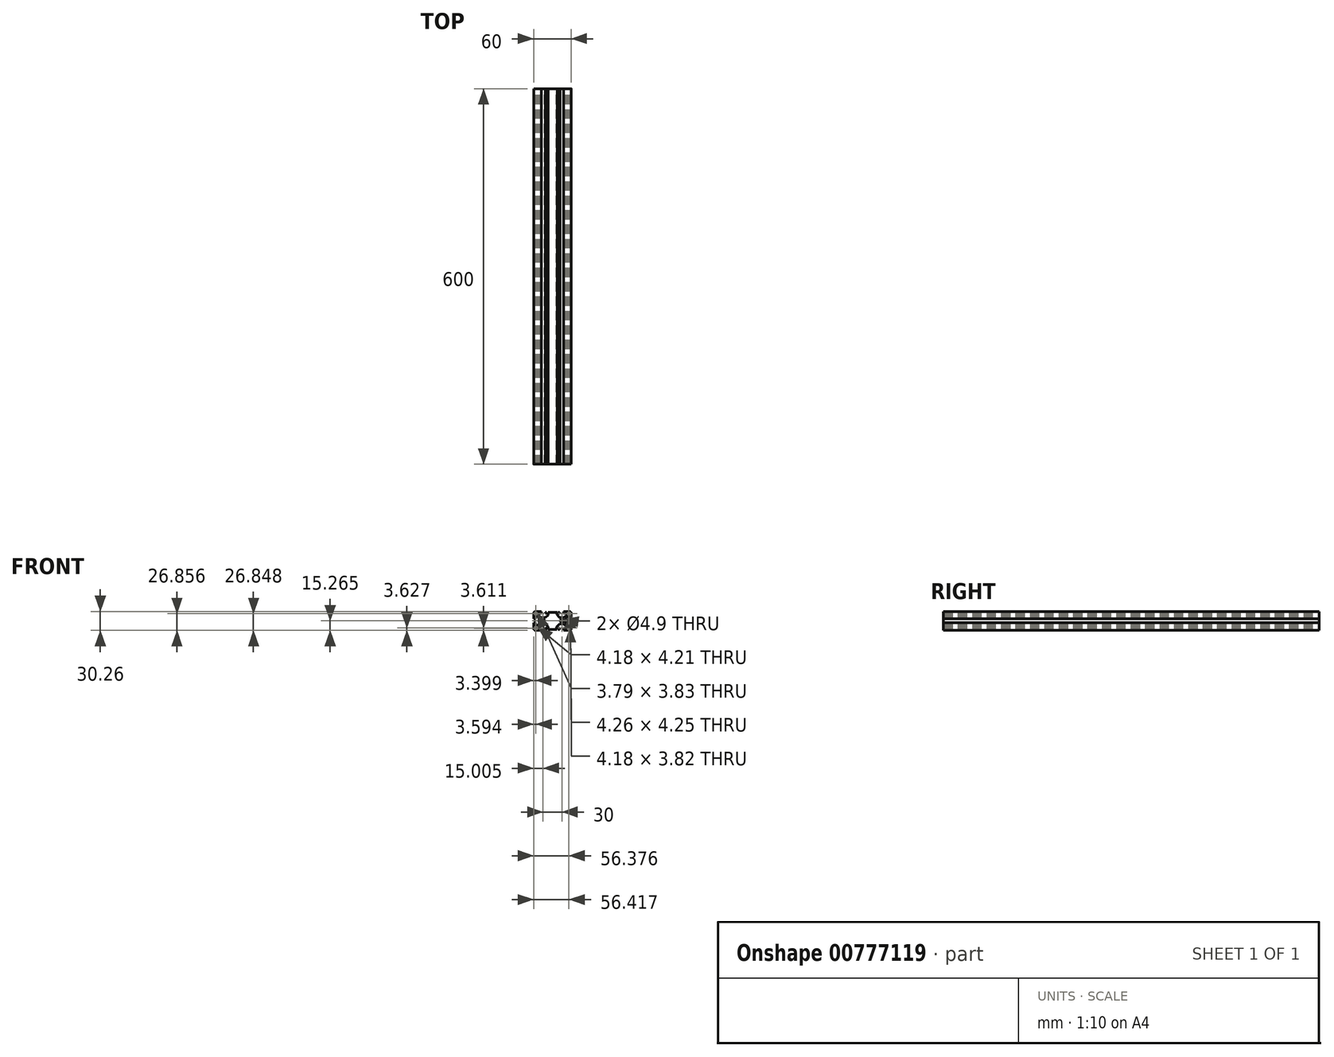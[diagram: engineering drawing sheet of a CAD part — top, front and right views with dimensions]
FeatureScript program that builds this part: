
annotation { "Feature Type Name" : "Feature", "Feature Type Description" : "" }
export const myFeature = defineFeature(function(context is Context, id is Id, definition is map)
    precondition{}
    {
        {
            var Q0;
            Q0=qCreatedBy(makeId("Front.planeOp"),FACE);
            var sketch = newSketch(context, id + "F0", { "sketchPlane" : qUnion([Q0])});
            skLineSegment(sketch, "E0.bottom", {"start": v(-62.13, 53.63) * mm, "end": v(-8.13, 53.63) * mm});
            skLineSegment(sketch, "E0.top", {"start": v(-62.13, 23.37) * mm, "end": v(-8.13, 23.37) * mm});
            skLineSegment(sketch, "E0.left", {"start": v(-65.13, 50.63) * mm, "end": v(-65.13, 26.37) * mm});
            skLineSegment(sketch, "E0.right", {"start": v(-5.13, 50.63) * mm, "end": v(-5.13, 26.37) * mm});
            skPoint(sketch, "E1.visualSharp", {"position": v(-65.13, 53.63) * mm});
            skArc(sketch, "E1.filletArc", {"start": v(-62.13, 53.63) * mm, "mid": v(-64.25, 52.76) * mm, "end": v(-65.13, 50.63) * mm});
            skPoint(sketch, "E2.visualSharp", {"position": v(-5.13, 53.63) * mm});
            skArc(sketch, "E2.filletArc", {"start": v(-5.13, 50.63) * mm, "mid": v(-6, 52.76) * mm, "end": v(-8.13, 53.63) * mm});
            skPoint(sketch, "E3.visualSharp", {"position": v(-5.13, 23.37) * mm});
            skArc(sketch, "E3.filletArc", {"start": v(-8.13, 23.37) * mm, "mid": v(-6, 24.25) * mm, "end": v(-5.13, 26.37) * mm});
            skPoint(sketch, "E4.visualSharp", {"position": v(-65.13, 23.37) * mm});
            skArc(sketch, "E4.filletArc", {"start": v(-65.13, 26.37) * mm, "mid": v(-64.25, 24.25) * mm, "end": v(-62.13, 23.37) * mm});
            skCircle(sketch, "E5", {"center": v(-50.13, 38.63) * mm, "radius": 2.45 * mm});
            skCircle(sketch, "E6", {"center": v(-20.13, 38.63) * mm, "radius": 2.45 * mm});
            skLineSegment(sketch, "E7.bottom", {"start": v(-62.63, 52.13) * mm, "end": v(-7.63, 52.13) * mm});
            skLineSegment(sketch, "E7.top", {"start": v(-62.63, 24.87) * mm, "end": v(-7.53, 24.87) * mm});
            skLineSegment(sketch, "E7.left", {"start": v(-63.63, 51.13) * mm, "end": v(-63.63, 25.87) * mm});
            skLineSegment(sketch, "E7.right", {"start": v(-6.63, 51.13) * mm, "end": v(-6.63, 25.77) * mm});
            skPoint(sketch, "E8.visualSharp", {"position": v(-6.63, 52.13) * mm});
            skArc(sketch, "E8.filletArc", {"start": v(-6.63, 51.13) * mm, "mid": v(-6.92, 51.84) * mm, "end": v(-7.63, 52.13) * mm});
            skPoint(sketch, "E9.visualSharp", {"position": v(-6.63, 24.87) * mm});
            skArc(sketch, "E9.filletArc", {"start": v(-7.53, 24.87) * mm, "mid": v(-6.89, 25.14) * mm, "end": v(-6.63, 25.77) * mm});
            skPoint(sketch, "E10.visualSharp", {"position": v(-63.63, 24.87) * mm});
            skArc(sketch, "E10.filletArc", {"start": v(-63.63, 25.87) * mm, "mid": v(-63.33, 25.17) * mm, "end": v(-62.63, 24.87) * mm});
            skPoint(sketch, "E11.visualSharp", {"position": v(-63.63, 52.13) * mm});
            skArc(sketch, "E11.filletArc", {"start": v(-62.63, 52.13) * mm, "mid": v(-63.33, 51.84) * mm, "end": v(-63.63, 51.13) * mm});
            skLineSegment(sketch, "E12.bottom", {"start": v(-59.84, 48.3) * mm, "end": v(-63.63, 48.3) * mm});
            skLineSegment(sketch, "E12.top", {"start": v(-59.84, 52.13) * mm, "end": v(-63.63, 52.13) * mm});
            skLineSegment(sketch, "E12.left", {"start": v(-59.84, 48.3) * mm, "end": v(-59.84, 52.13) * mm});
            skLineSegment(sketch, "E12.right", {"start": v(-63.63, 48.3) * mm, "end": v(-63.63, 52.13) * mm});
            skLineSegment(sketch, "E13.bottom", {"start": v(-59.45, 29.09) * mm, "end": v(-63.63, 29.09) * mm});
            skLineSegment(sketch, "E13.top", {"start": v(-59.45, 24.87) * mm, "end": v(-63.63, 24.87) * mm});
            skLineSegment(sketch, "E13.left", {"start": v(-59.45, 29.09) * mm, "end": v(-59.45, 24.87) * mm});
            skLineSegment(sketch, "E13.right", {"start": v(-63.63, 29.09) * mm, "end": v(-63.63, 24.87) * mm});
            skLineSegment(sketch, "E14.bottom", {"start": v(-10.88, 29.12) * mm, "end": v(-6.63, 29.12) * mm});
            skLineSegment(sketch, "E14.top", {"start": v(-10.88, 24.87) * mm, "end": v(-6.63, 24.87) * mm});
            skLineSegment(sketch, "E14.left", {"start": v(-10.88, 29.12) * mm, "end": v(-10.88, 24.87) * mm});
            skLineSegment(sketch, "E14.right", {"start": v(-6.63, 29.12) * mm, "end": v(-6.63, 24.87) * mm});
            skLineSegment(sketch, "E15.bottom", {"start": v(-6.63, 52.13) * mm, "end": v(-10.8, 52.13) * mm});
            skLineSegment(sketch, "E15.top", {"start": v(-6.63, 48.32) * mm, "end": v(-10.8, 48.32) * mm});
            skLineSegment(sketch, "E15.left", {"start": v(-6.63, 52.13) * mm, "end": v(-6.63, 48.32) * mm});
            skLineSegment(sketch, "E15.right", {"start": v(-10.8, 52.13) * mm, "end": v(-10.8, 48.32) * mm});
            skLineSegment(sketch, "E16.bottom", {"start": v(-55.91, 50.63) * mm, "end": v(-53.07, 50.63) * mm});
            skLineSegment(sketch, "E16.top", {"start": v(-55.91, 52.13) * mm, "end": v(-53.07, 52.13) * mm});
            skLineSegment(sketch, "E16.left", {"start": v(-55.91, 50.63) * mm, "end": v(-55.91, 52.13) * mm});
            skLineSegment(sketch, "E16.right", {"start": v(-53.07, 50.63) * mm, "end": v(-53.07, 52.13) * mm});
            skLineSegment(sketch, "E17.bottom", {"start": v(-44.63, 50.63) * mm, "end": v(-46.61, 50.63) * mm});
            skLineSegment(sketch, "E17.top", {"start": v(-44.63, 52.13) * mm, "end": v(-46.61, 52.13) * mm});
            skLineSegment(sketch, "E17.left", {"start": v(-44.63, 50.63) * mm, "end": v(-44.63, 52.13) * mm});
            skLineSegment(sketch, "E17.right", {"start": v(-46.61, 50.63) * mm, "end": v(-46.61, 52.13) * mm});
            skLineSegment(sketch, "E18.bottom", {"start": v(-26.48, 50.63) * mm, "end": v(-23.47, 50.63) * mm});
            skLineSegment(sketch, "E18.top", {"start": v(-26.48, 52.13) * mm, "end": v(-23.47, 52.13) * mm});
            skLineSegment(sketch, "E18.left", {"start": v(-26.48, 50.63) * mm, "end": v(-26.48, 52.13) * mm});
            skLineSegment(sketch, "E18.right", {"start": v(-23.47, 50.63) * mm, "end": v(-23.47, 52.13) * mm});
            skLineSegment(sketch, "E19.bottom", {"start": v(-14.95, 50.63) * mm, "end": v(-17.1, 50.63) * mm});
            skLineSegment(sketch, "E19.top", {"start": v(-14.95, 52.13) * mm, "end": v(-17.1, 52.13) * mm});
            skLineSegment(sketch, "E19.left", {"start": v(-14.95, 50.63) * mm, "end": v(-14.95, 52.13) * mm});
            skLineSegment(sketch, "E19.right", {"start": v(-17.1, 50.63) * mm, "end": v(-17.1, 52.13) * mm});
            skLineSegment(sketch, "E20.bottom", {"start": v(-8.13, 44.16) * mm, "end": v(-6.63, 44.16) * mm});
            skLineSegment(sketch, "E20.top", {"start": v(-8.13, 41.83) * mm, "end": v(-6.63, 41.83) * mm});
            skLineSegment(sketch, "E20.left", {"start": v(-8.13, 44.16) * mm, "end": v(-8.13, 41.83) * mm});
            skLineSegment(sketch, "E20.right", {"start": v(-6.63, 44.16) * mm, "end": v(-6.63, 41.83) * mm});
            skLineSegment(sketch, "E21.bottom", {"start": v(-8.13, 32.88) * mm, "end": v(-6.63, 32.88) * mm});
            skLineSegment(sketch, "E21.top", {"start": v(-8.13, 35.38) * mm, "end": v(-6.63, 35.38) * mm});
            skLineSegment(sketch, "E21.left", {"start": v(-8.13, 32.88) * mm, "end": v(-8.13, 35.38) * mm});
            skLineSegment(sketch, "E21.right", {"start": v(-6.63, 32.88) * mm, "end": v(-6.63, 35.38) * mm});
            skLineSegment(sketch, "E22.bottom", {"start": v(-14.8, 26.37) * mm, "end": v(-17.1, 26.37) * mm});
            skLineSegment(sketch, "E22.top", {"start": v(-14.8, 24.87) * mm, "end": v(-17.1, 24.87) * mm});
            skLineSegment(sketch, "E22.left", {"start": v(-14.8, 26.37) * mm, "end": v(-14.8, 24.87) * mm});
            skLineSegment(sketch, "E22.right", {"start": v(-17.1, 26.37) * mm, "end": v(-17.1, 24.87) * mm});
            skLineSegment(sketch, "E23.bottom", {"start": v(-26.1, 26.37) * mm, "end": v(-23.56, 26.37) * mm});
            skLineSegment(sketch, "E23.top", {"start": v(-26.1, 24.87) * mm, "end": v(-23.56, 24.87) * mm});
            skLineSegment(sketch, "E23.left", {"start": v(-26.1, 26.37) * mm, "end": v(-26.1, 24.87) * mm});
            skLineSegment(sketch, "E23.right", {"start": v(-23.56, 26.37) * mm, "end": v(-23.56, 24.87) * mm});
            skLineSegment(sketch, "E24.bottom", {"start": v(-44.16, 26.37) * mm, "end": v(-46.61, 26.37) * mm});
            skLineSegment(sketch, "E24.top", {"start": v(-44.16, 24.87) * mm, "end": v(-46.61, 24.87) * mm});
            skLineSegment(sketch, "E24.left", {"start": v(-44.16, 26.37) * mm, "end": v(-44.16, 24.87) * mm});
            skLineSegment(sketch, "E24.right", {"start": v(-46.61, 26.37) * mm, "end": v(-46.61, 24.87) * mm});
            skLineSegment(sketch, "E25.bottom", {"start": v(-55.52, 26.37) * mm, "end": v(-53.07, 26.37) * mm});
            skLineSegment(sketch, "E25.top", {"start": v(-55.52, 24.87) * mm, "end": v(-53.07, 24.87) * mm});
            skLineSegment(sketch, "E25.left", {"start": v(-55.52, 26.37) * mm, "end": v(-55.52, 24.87) * mm});
            skLineSegment(sketch, "E25.right", {"start": v(-53.07, 26.37) * mm, "end": v(-53.07, 24.87) * mm});
            skLineSegment(sketch, "E26.bottom", {"start": v(-62.13, 33.01) * mm, "end": v(-63.63, 33.01) * mm});
            skLineSegment(sketch, "E26.top", {"start": v(-62.13, 35.38) * mm, "end": v(-63.63, 35.38) * mm});
            skLineSegment(sketch, "E26.left", {"start": v(-62.13, 33.01) * mm, "end": v(-62.13, 35.38) * mm});
            skLineSegment(sketch, "E26.right", {"start": v(-63.63, 33.01) * mm, "end": v(-63.63, 35.38) * mm});
            skLineSegment(sketch, "E27.bottom", {"start": v(-62.13, 44.3) * mm, "end": v(-63.63, 44.3) * mm});
            skLineSegment(sketch, "E27.top", {"start": v(-62.13, 41.83) * mm, "end": v(-63.63, 41.83) * mm});
            skLineSegment(sketch, "E27.left", {"start": v(-62.13, 44.3) * mm, "end": v(-62.13, 41.83) * mm});
            skLineSegment(sketch, "E27.right", {"start": v(-63.63, 44.3) * mm, "end": v(-63.63, 41.83) * mm});
            skLineSegment(sketch, "E28", {"start": v(-57.98, 52.13) * mm, "end": v(-57.98, 48.56) * mm});
            skLineSegment(sketch, "E29", {"start": v(-57.98, 48.56) * mm, "end": v(-53.64, 43.99) * mm});
            skLineSegment(sketch, "E30", {"start": v(-53.64, 43.99) * mm, "end": v(-46.61, 43.99) * mm});
            skLineSegment(sketch, "E31", {"start": v(-46.61, 43.99) * mm, "end": v(-41.95, 47.75) * mm});
            skLineSegment(sketch, "E32", {"start": v(-41.95, 47.75) * mm, "end": v(-41.95, 52.13) * mm});
            skLineSegment(sketch, "E33", {"start": v(-38.1, 52.13) * mm, "end": v(-40.07, 50.6) * mm});
            skLineSegment(sketch, "E34", {"start": v(-40.07, 50.6) * mm, "end": v(-40.07, 48) * mm});
            skLineSegment(sketch, "E35", {"start": v(-40.07, 48) * mm, "end": v(-41.13, 46.11) * mm});
            skLineSegment(sketch, "E36", {"start": v(-41.13, 46.11) * mm, "end": v(-44.24, 43) * mm});
            skLineSegment(sketch, "E37", {"start": v(-44.24, 43) * mm, "end": v(-45.06, 41.7) * mm});
            skLineSegment(sketch, "E38", {"start": v(-45.06, 41.7) * mm, "end": v(-45.06, 35.9) * mm});
            skLineSegment(sketch, "E39", {"start": v(-45.06, 35.9) * mm, "end": v(-44.08, 34.26) * mm});
            skLineSegment(sketch, "E40", {"start": v(-44.08, 34.26) * mm, "end": v(-40.89, 30.99) * mm});
            skLineSegment(sketch, "E41", {"start": v(-40.89, 30.99) * mm, "end": v(-39.99, 29.1) * mm});
            skLineSegment(sketch, "E42", {"start": v(-39.99, 29.1) * mm, "end": v(-39.99, 27.63) * mm});
            skLineSegment(sketch, "E43", {"start": v(-39.99, 27.63) * mm, "end": v(-39.25, 26.33) * mm});
            skLineSegment(sketch, "E44", {"start": v(-39.25, 26.33) * mm, "end": v(-38.35, 24.87) * mm});
            skLineSegment(sketch, "E45", {"start": v(-63.63, 45.6) * mm, "end": v(-62.86, 46.67) * mm});
            skLineSegment(sketch, "E46", {"start": v(-62.86, 46.67) * mm, "end": v(-60.08, 46.67) * mm});
            skLineSegment(sketch, "E47", {"start": v(-60.08, 46.67) * mm, "end": v(-55.42, 42.58) * mm});
            skLineSegment(sketch, "E48", {"start": v(-55.42, 42.58) * mm, "end": v(-55.42, 35.06) * mm});
            skLineSegment(sketch, "E49", {"start": v(-55.42, 35.06) * mm, "end": v(-60, 30.48) * mm});
            skLineSegment(sketch, "E50", {"start": v(-60, 30.48) * mm, "end": v(-63.03, 30.48) * mm});
            skLineSegment(sketch, "E51", {"start": v(-63.03, 30.48) * mm, "end": v(-63.63, 31.46) * mm});
            skLineSegment(sketch, "E52", {"start": v(-32.06, 52.13) * mm, "end": v(-30.26, 50.85) * mm});
            skLineSegment(sketch, "E53", {"start": v(-30.26, 50.46) * mm, "end": v(-30.26, 48.33) * mm});
            skLineSegment(sketch, "E54", {"start": v(-30.26, 48.33) * mm, "end": v(-29.44, 46.13) * mm});
            skLineSegment(sketch, "E55", {"start": v(-29.44, 46.13) * mm, "end": v(-26.1, 42.94) * mm});
            skLineSegment(sketch, "E56", {"start": v(-26.1, 42.94) * mm, "end": v(-25.35, 41.47) * mm});
            skLineSegment(sketch, "E57", {"start": v(-25.35, 41.47) * mm, "end": v(-25.35, 35.17) * mm});
            skLineSegment(sketch, "E58", {"start": v(-25.35, 35.17) * mm, "end": v(-26.42, 33.7) * mm});
            skLineSegment(sketch, "E59", {"start": v(-26.42, 33.7) * mm, "end": v(-29.44, 30.51) * mm});
            skLineSegment(sketch, "E60", {"start": v(-29.44, 30.51) * mm, "end": v(-30.26, 28.55) * mm});
            skLineSegment(sketch, "E61", {"start": v(-30.26, 28.55) * mm, "end": v(-30.26, 26.91) * mm});
            skLineSegment(sketch, "E62", {"start": v(-30.26, 26.91) * mm, "end": v(-31.9, 24.87) * mm});
            skLineSegment(sketch, "E63", {"start": v(-57.4, 24.87) * mm, "end": v(-58.14, 25.93) * mm});
            skLineSegment(sketch, "E64", {"start": v(-58.14, 25.93) * mm, "end": v(-58.14, 28.71) * mm});
            skLineSegment(sketch, "E65", {"start": v(-58.14, 28.71) * mm, "end": v(-53.4, 33.45) * mm});
            skLineSegment(sketch, "E66", {"start": v(-53.4, 33.45) * mm, "end": v(-46.61, 33.45) * mm});
            skLineSegment(sketch, "E67", {"start": v(-46.61, 33.45) * mm, "end": v(-41.79, 29.12) * mm});
            skLineSegment(sketch, "E68", {"start": v(-41.79, 29.12) * mm, "end": v(-41.79, 25.69) * mm});
            skLineSegment(sketch, "E69", {"start": v(-41.79, 25.69) * mm, "end": v(-41.79, 24.87) * mm});
            skLineSegment(sketch, "E70", {"start": v(-27.56, 52.13) * mm, "end": v(-28.24, 51.5) * mm});
            skLineSegment(sketch, "E71", {"start": v(-28.24, 51.5) * mm, "end": v(-28.24, 48.65) * mm});
            skLineSegment(sketch, "E72", {"start": v(-28.24, 48.65) * mm, "end": v(-24.08, 44.25) * mm});
            skLineSegment(sketch, "E73", {"start": v(-24.08, 44.25) * mm, "end": v(-23.22, 43.64) * mm});
            skLineSegment(sketch, "E74", {"start": v(-23.22, 43.64) * mm, "end": v(-17.5, 43.64) * mm});
            skLineSegment(sketch, "E75", {"start": v(-17.5, 43.64) * mm, "end": v(-13.1, 46.68) * mm});
            skLineSegment(sketch, "E76", {"start": v(-13.1, 46.68) * mm, "end": v(-11.98, 48.25) * mm});
            skLineSegment(sketch, "E77", {"start": v(-11.98, 48.25) * mm, "end": v(-11.98, 51.5) * mm});
            skLineSegment(sketch, "E78", {"start": v(-11.98, 51.5) * mm, "end": v(-12.86, 52.13) * mm});
            skLineSegment(sketch, "E79", {"start": v(-27.8, 24.87) * mm, "end": v(-28.62, 26.26) * mm});
            skLineSegment(sketch, "E80", {"start": v(-28.62, 26.26) * mm, "end": v(-28.62, 28.55) * mm});
            skLineSegment(sketch, "E81", {"start": v(-28.62, 28.55) * mm, "end": v(-23.72, 33.45) * mm});
            skLineSegment(sketch, "E82", {"start": v(-23.72, 33.45) * mm, "end": v(-17.18, 33.45) * mm});
            skLineSegment(sketch, "E83", {"start": v(-17.18, 33.45) * mm, "end": v(-12.35, 29.53) * mm});
            skLineSegment(sketch, "E84", {"start": v(-12.35, 29.53) * mm, "end": v(-12.35, 26.18) * mm});
            skLineSegment(sketch, "E85", {"start": v(-12.35, 26.18) * mm, "end": v(-13.1, 24.87) * mm});
            skLineSegment(sketch, "E86", {"start": v(-6.63, 46.81) * mm, "end": v(-9.92, 46.81) * mm});
            skLineSegment(sketch, "E87", {"start": v(-9.92, 46.81) * mm, "end": v(-14.58, 42.15) * mm});
            skLineSegment(sketch, "E88", {"start": v(-14.58, 42.15) * mm, "end": v(-14.58, 35.29) * mm});
            skLineSegment(sketch, "E89", {"start": v(-14.58, 35.29) * mm, "end": v(-10.5, 30.79) * mm});
            skLineSegment(sketch, "E90", {"start": v(-10.5, 30.79) * mm, "end": v(-6.63, 30.79) * mm});
            skLineSegment(sketch, "E91.bottom", {"start": v(-63.63, 41.83) * mm, "end": v(-65.13, 41.83) * mm});
            skLineSegment(sketch, "E91.top", {"start": v(-63.63, 35.29) * mm, "end": v(-65.13, 35.29) * mm});
            skLineSegment(sketch, "E91.left", {"start": v(-63.63, 41.83) * mm, "end": v(-63.63, 35.29) * mm});
            skLineSegment(sketch, "E91.right", {"start": v(-65.13, 41.83) * mm, "end": v(-65.13, 35.29) * mm});
            skLineSegment(sketch, "E92.bottom", {"start": v(-53.07, 52.13) * mm, "end": v(-46.61, 52.13) * mm});
            skLineSegment(sketch, "E92.top", {"start": v(-53.07, 53.63) * mm, "end": v(-46.61, 53.63) * mm});
            skLineSegment(sketch, "E92.left", {"start": v(-53.07, 52.13) * mm, "end": v(-53.07, 53.63) * mm});
            skLineSegment(sketch, "E92.right", {"start": v(-46.61, 52.13) * mm, "end": v(-46.61, 53.63) * mm});
            skLineSegment(sketch, "E93.bottom", {"start": v(-23.47, 52.13) * mm, "end": v(-17.1, 52.13) * mm});
            skLineSegment(sketch, "E93.top", {"start": v(-23.47, 53.63) * mm, "end": v(-17.1, 53.63) * mm});
            skLineSegment(sketch, "E93.left", {"start": v(-23.47, 52.13) * mm, "end": v(-23.47, 53.63) * mm});
            skLineSegment(sketch, "E93.right", {"start": v(-17.1, 52.13) * mm, "end": v(-17.1, 53.63) * mm});
            skLineSegment(sketch, "E94.bottom", {"start": v(-6.63, 41.83) * mm, "end": v(-5.13, 41.83) * mm});
            skLineSegment(sketch, "E94.top", {"start": v(-6.63, 35.29) * mm, "end": v(-5.13, 35.29) * mm});
            skLineSegment(sketch, "E94.left", {"start": v(-6.63, 41.83) * mm, "end": v(-6.63, 35.29) * mm});
            skLineSegment(sketch, "E94.right", {"start": v(-5.13, 41.83) * mm, "end": v(-5.13, 35.29) * mm});
            skLineSegment(sketch, "E95.bottom", {"start": v(-17.1, 24.87) * mm, "end": v(-23.47, 24.87) * mm});
            skLineSegment(sketch, "E95.top", {"start": v(-17.1, 23.37) * mm, "end": v(-23.47, 23.37) * mm});
            skLineSegment(sketch, "E95.left", {"start": v(-17.1, 24.87) * mm, "end": v(-17.1, 23.37) * mm});
            skLineSegment(sketch, "E95.right", {"start": v(-23.47, 24.87) * mm, "end": v(-23.47, 23.37) * mm});
            skLineSegment(sketch, "E96.bottom", {"start": v(-46.61, 24.87) * mm, "end": v(-53.07, 24.87) * mm});
            skLineSegment(sketch, "E96.top", {"start": v(-46.61, 23.37) * mm, "end": v(-53.07, 23.37) * mm});
            skLineSegment(sketch, "E96.left", {"start": v(-46.61, 24.87) * mm, "end": v(-46.61, 23.37) * mm});
            skLineSegment(sketch, "E96.right", {"start": v(-53.07, 24.87) * mm, "end": v(-53.07, 23.37) * mm});
            skSolve(sketch);
        }
        {
            var Q0;
            {var subQ12=sQuery(id+"F0.wireOp",EDGE,"E1.filletArc");Q0=makeQuery(id+"F0.imprint","IMPRINT",FACE,{"disambiguationData":[TD([[makeQuery(id+"F0.imprint","IMPRINT",EDGE,{"derivedFrom":subQ12}),1.0]])]});}
            var Q1;
            {var subQ4=sQuery(id+"F0.wireOp",EDGE,"E17.top");Q1=makeQuery(id+"F0.imprint","IMPRINT",FACE,{"disambiguationData":[TD([[makeQuery(id+"F0.imprint","IMPRINT",EDGE,{"derivedFrom":subQ4}),-1.0]])]});}
            var Q2;
            {var subQ13=sQuery(id+"F0.wireOp",EDGE,"E2.filletArc");Q2=makeQuery(id+"F0.imprint","IMPRINT",FACE,{"disambiguationData":[TD([[makeQuery(id+"F0.imprint","IMPRINT",EDGE,{"derivedFrom":subQ13}),1.0]])]});}
            var Q3;
            {var subQ13=sQuery(id+"F0.wireOp",EDGE,"E4.filletArc");Q3=makeQuery(id+"F0.imprint","IMPRINT",FACE,{"disambiguationData":[TD([[makeQuery(id+"F0.imprint","IMPRINT",EDGE,{"derivedFrom":subQ13}),1.0]])]});}
            var Q4;
            {var subQ0=sQuery(id+"F0.wireOp",EDGE,"E23.top");Q4=makeQuery(id+"F0.imprint","IMPRINT",FACE,{"disambiguationData":[TD([[makeQuery(id+"F0.imprint","IMPRINT",EDGE,{"derivedFrom":subQ0}),-1.0]])]});}
            var Q5;
            {var subQ13=sQuery(id+"F0.wireOp",EDGE,"E3.filletArc");Q5=makeQuery(id+"F0.imprint","IMPRINT",FACE,{"disambiguationData":[TD([[makeQuery(id+"F0.imprint","IMPRINT",EDGE,{"derivedFrom":subQ13}),1.0]])]});}
            var Q6;
            Q6=makeQuery(id+"F0.imprint","IMPRINT",FACE,{"disambiguationData":[TD([[makeQuery(id+"F0.imprint","IMPRINT",EDGE,{"derivedFrom":sQuery(id+"F0.wireOp",EDGE,"E6")}),-1.0]])]});
            var Q7;
            Q7=makeQuery(id+"F0.imprint","IMPRINT",FACE,{"disambiguationData":[TD([[makeQuery(id+"F0.imprint","IMPRINT",EDGE,{"derivedFrom":sQuery(id+"F0.wireOp",EDGE,"E5")}),-1.0]])]});
            var Q8;
            Q8=makeQuery(id+"F0.imprint","IMPRINT",FACE,{"disambiguationData":[TD([[makeQuery(id+"F0.imprint","IMPRINT",EDGE,{"derivedFrom":sQuery(id+"F0.wireOp",EDGE,"E17.bottom")}),-1.0]])]});
            var Q9;
            Q9=makeQuery(id+"F0.imprint","IMPRINT",FACE,{"disambiguationData":[TD([[makeQuery(id+"F0.imprint","IMPRINT",EDGE,{"derivedFrom":sQuery(id+"F0.wireOp",EDGE,"E16.bottom")}),1.0]])]});
            var Q10;
            Q10=makeQuery(id+"F0.imprint","IMPRINT",FACE,{"disambiguationData":[TD([[makeQuery(id+"F0.imprint","IMPRINT",EDGE,{"derivedFrom":sQuery(id+"F0.wireOp",EDGE,"E27.bottom")}),1.0]])]});
            var Q11;
            Q11=makeQuery(id+"F0.imprint","IMPRINT",FACE,{"disambiguationData":[TD([[makeQuery(id+"F0.imprint","IMPRINT",EDGE,{"derivedFrom":sQuery(id+"F0.wireOp",EDGE,"E26.bottom")}),-1.0]])]});
            var Q12;
            Q12=makeQuery(id+"F0.imprint","IMPRINT",FACE,{"disambiguationData":[TD([[makeQuery(id+"F0.imprint","IMPRINT",EDGE,{"derivedFrom":sQuery(id+"F0.wireOp",EDGE,"E25.bottom")}),-1.0]])]});
            var Q13;
            Q13=makeQuery(id+"F0.imprint","IMPRINT",FACE,{"disambiguationData":[TD([[makeQuery(id+"F0.imprint","IMPRINT",EDGE,{"derivedFrom":sQuery(id+"F0.wireOp",EDGE,"E24.bottom")}),1.0]])]});
            var Q14;
            Q14=makeQuery(id+"F0.imprint","IMPRINT",FACE,{"disambiguationData":[TD([[makeQuery(id+"F0.imprint","IMPRINT",EDGE,{"derivedFrom":sQuery(id+"F0.wireOp",EDGE,"E23.bottom")}),-1.0]])]});
            var Q15;
            Q15=makeQuery(id+"F0.imprint","IMPRINT",FACE,{"disambiguationData":[TD([[makeQuery(id+"F0.imprint","IMPRINT",EDGE,{"derivedFrom":sQuery(id+"F0.wireOp",EDGE,"E22.bottom")}),1.0]])]});
            var Q16;
            Q16=makeQuery(id+"F0.imprint","IMPRINT",FACE,{"disambiguationData":[TD([[makeQuery(id+"F0.imprint","IMPRINT",EDGE,{"derivedFrom":sQuery(id+"F0.wireOp",EDGE,"E21.bottom")}),1.0]])]});
            var Q17;
            Q17=makeQuery(id+"F0.imprint","IMPRINT",FACE,{"disambiguationData":[TD([[makeQuery(id+"F0.imprint","IMPRINT",EDGE,{"derivedFrom":sQuery(id+"F0.wireOp",EDGE,"E20.bottom")}),-1.0]])]});
            var Q18;
            Q18=makeQuery(id+"F0.imprint","IMPRINT",FACE,{"disambiguationData":[TD([[makeQuery(id+"F0.imprint","IMPRINT",EDGE,{"derivedFrom":sQuery(id+"F0.wireOp",EDGE,"E19.bottom")}),-1.0]])]});
            var Q19;
            Q19=makeQuery(id+"F0.imprint","IMPRINT",FACE,{"disambiguationData":[TD([[makeQuery(id+"F0.imprint","IMPRINT",EDGE,{"derivedFrom":sQuery(id+"F0.wireOp",EDGE,"E18.bottom")}),1.0]])]});
            extrude(context, id + "F1", {"entities" : qUnion([Q0, Q1, Q2, Q3, Q4, Q5, Q6, Q7, Q8, Q9, Q10, Q11, Q12, Q13, Q14, Q15, Q16, Q17, Q18, Q19]), "depth" : 600 * mm, "offsetDistance" : 25 * mm});
        }
    });
